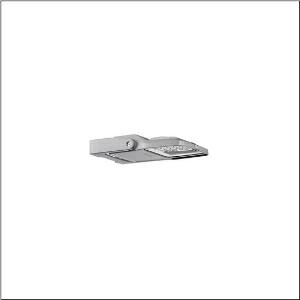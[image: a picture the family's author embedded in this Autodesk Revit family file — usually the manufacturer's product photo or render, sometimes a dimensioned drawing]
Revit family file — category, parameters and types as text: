
# Revit family: floodlight_fl_21_iq_micro___pl52_5xa7762a2d2a_5d06
name_source: partatom
category: Lighting Fixtures
units: mm (PartAtom-declared; Revit-internal decimal feet)

## family parameters
Cut with Voids When Loaded = No
Host = Face
Light Source = No
Part Type = Normal
Room Calculation Point = No
Round Connector Dimension = Use Diameter
Shared = No

## types (1)
- --- (1 x LED, 2890 lm, 23.1 W, 3000K)
    Apparent Load = 23 VA
    CIE Flux Codes = 26 60 98 100 100
    Color Rendering = 70
    Color Temperature = 3000K
    Default Elevation = 1800 mm
    Description = Floodlight FL 21 iQ micro, floodlight, primary light control with lens, of PMMA, primary optical cover: protective disc, of toughened safety glass, transparent, light distribution: PL52, light emission: direct distribution, installation type: surface-mounted, LED, High Power LED, rated luminous flux: 2.890lm, luminous efficacy: 125lm/W, light colour: 730, colour temperature: 3000K, control: Auto-Match, Temp-Guard, Night-Set, Smart-Wire, Desk-Remote (wireless, voltage-free reading and setting of iQ features in the workshop via application-optimized NFC function/RFID function), optimised constant luminous flux control (CLO 2.0), Street-Remote, with terminal, 6-pole, mains connection: 220..240V, AC, 50/60Hz, start of lifetime: 23W, end of service life: 24W, reduction: 11W, luminaire housing, of diecast aluminium, powder-coated, Siteco® metallic grey (DB 702S), corrosivity category C5 mid according to DIN EN ISO 12944, sealing non-destructively replaceable, design bracket, of diecast aluminium, powder-coated, Siteco® metallic grey (DB 702S), protection rating (complete): IP66, insulation class (complete): insulation class II (safety insulation), certification: CE, ENEC, VDE, protection symbol: D, impact resistance: IK07, permissible operating ambient temperature: -40..+40°C, permissible operating ambient temperature for outdoor applications: -40..+50°C, standard: DIN EN 12944, LABS conformity tested according to VDMA 24364:2018-05, packaging unit: 1 piece

Light Distribution: PL52
    Height = 65 mm
    Lamp = 1 x LED
    Lamp Light Flux = 2890 lm
    Lamp Power = 23.1 W
    Lamp count = 1
    Length = 312 mm
    Luminous efficacy = 125 lm/W
    Manufacturer = Siteco
    ModVariant = No
    Model = 5XA7762A2D2A
    Mounting Place = Wall
    Mounting Type = Surface mounted
    Number of Poles = 1
    OnlyDefault = Yes
    Power Factor = 1
    Product Name = Floodlight FL 21 iQ micro | PL52
    Product group = floodlight | wall mounted
    ProductGroupID = 2001
    Protection Class = Protection class II
    Protection Degree = IP 66
    RLX_Detail_Level = 1
    RLX_Emergency_Light_Flux = 0 lm
    RLX_Emergency_Type = 0
    RLX_Emergency_Type_DB = No
    RlxData = <blob elided: 97589 chars, md5=0b039728>
    Socket = socket
    Standby Power = 0 W
    System Light Flux = 2890 lm
    System Power = 23 W
    Type Comments = factory setting: luminous flux: 100 % | dim-lin: 254 | 455 mA
    Type Image = l_1006878.jpg
    URL = http://relux.com
    VarID = @adj_149167
    Voltage = 0 V
    Weight = 0.00 kg
    Width = 230 mm

## geometry (parser evidence)
native form markers: Blend x4, Sweep x11
no freeform markers — native parametric forms only
